# Revit family: 0042289 Lighting Fixture_Sylvania_HSX Syl-Line_Surface Mounted
name_source: partatom
category: Lighting Fixtures
revit_build: Autodesk Revit 2017 (Build: 20190507_1515(x64)
units: mm (PartAtom-declared; Revit-internal decimal feet)

## family parameters
Cut with Voids When Loaded = No
Host = Face
Light Source = Yes
OmniClass Number = 23.80.70.11.17
OmniClass Title = Specialized Lighting by Location or Use
Part Type = Normal
Room Calculation Point = No
Round Connector Dimension = Use Diameter
Shared = No

## types (1)
- HSXSYL  LED NW DALI 1720 EM WB
    Apparent Load = 75 VA
    Assembly Code = D5020200
    Body Material = Plastic_Sylvania_HSX Syl-Line_White
    Bracket Height = 94 mm
    Bracket Width = 70.6 mm  [stored 0.231627 ft]
    CRI (Ra) = >80
    Cap Material = Plastic_Sylvania_HSX Syl-Line_White
    Catalog Number = 0042289 HSXSYL  LED NW DALI 1720 EM WB
    Color Filter = 16777215
    Default Elevation = 0 mm  [stored 0 ft]
    Description = 72W and 75W LED surface and suspended luminaires HSX Syl-Line is perfect for retail, industry, manufacturing, airports or data centres Extended offering of alternative optics for Syl-Line trunking Available with a white sheet steel reflector and a PMMA Diffuser Available in 1,720mm (same length as standard Syl-Line gear trays and trunking) High performance: delivers 6,660lm (luminaire lumen output on 72W version), equating to 93lm/W (total system efficiency) Available in neutral white (4,000K) Integrated LED solution that has the same aesthetics as the fluorescent version (non dotting) Energy efficient electronic gear including Analogue 1-10V dimmable, DALI dimmable and 3 hour emergency versions as standard Ease of installation through the plug connector Innovative clip design allows quick and simple installation of the electrical unit (average installation time of the gear tray at just over a minute) Energy class: A++, A+, A Long lifetime: 50,000 hours life at 70% of the original output L70
    Diffuser Material = Polycarbonate_Sylvania_HSX Syl-Line_4000K
    Dimming Lamp Color Temperature Shift = <None>
    Drive Current = 350mA
    Electrical Protection = CLASS I
    Emit from Line Length = 1700 mm  [stored 5.57743 ft]
    Glow Wire Test = 650 °C
    Height = 167.5 mm  [stored 0.549541 ft]
    IK Rating = IK02
    IP Rating = IP20
    Inrush Current (max. quantity per 16A C breaker) = 10
    LOR = 100%
    Lamp = Integrated LED
    Length = 1720 mm
    Life = 50 000h
    Line End Left = 300 mm
    Line End Right = 20 mm  [stored 0.0656168 ft]
    Manufacturer = Feilo Sylvania
    Model = HSXSYL  LED NW DALI 1720 EM WB
    Mounting Material = Steel_Sylvania_HSX Syl-Line_White
    Photometric Web File = 0042289_HSXSYLLEDNWDALI1720EMWB-192721.ies
    Product Family = HSX SYL-LINE
    Product Page URL = http://www.sylvania-lighting.com
    T Class Max = 25 °C
    T Class Min = -10 °C
    Ta Rating = -10°C to +25°C
    Tilt Angle = -90.00°
    Trucking Material = Steel_Sylvania_HSX Syl-Line_White
    URL = http://www.sylvania-lighting.com
    Voltage = 230 V
    Voltage Comments = UNV (Universal Voltage; 220-240 Volt)
    Weight = 6.50 kg
    Width = 164 mm  [stored 0.538058 ft]

note: [stored X ft] marks values corroborated as IEEE doubles in the binary element streams (Revit-internal decimal feet)

## geometry (parser evidence)
native form markers: Blend x4, Sweep x7
no freeform markers — native parametric forms only
